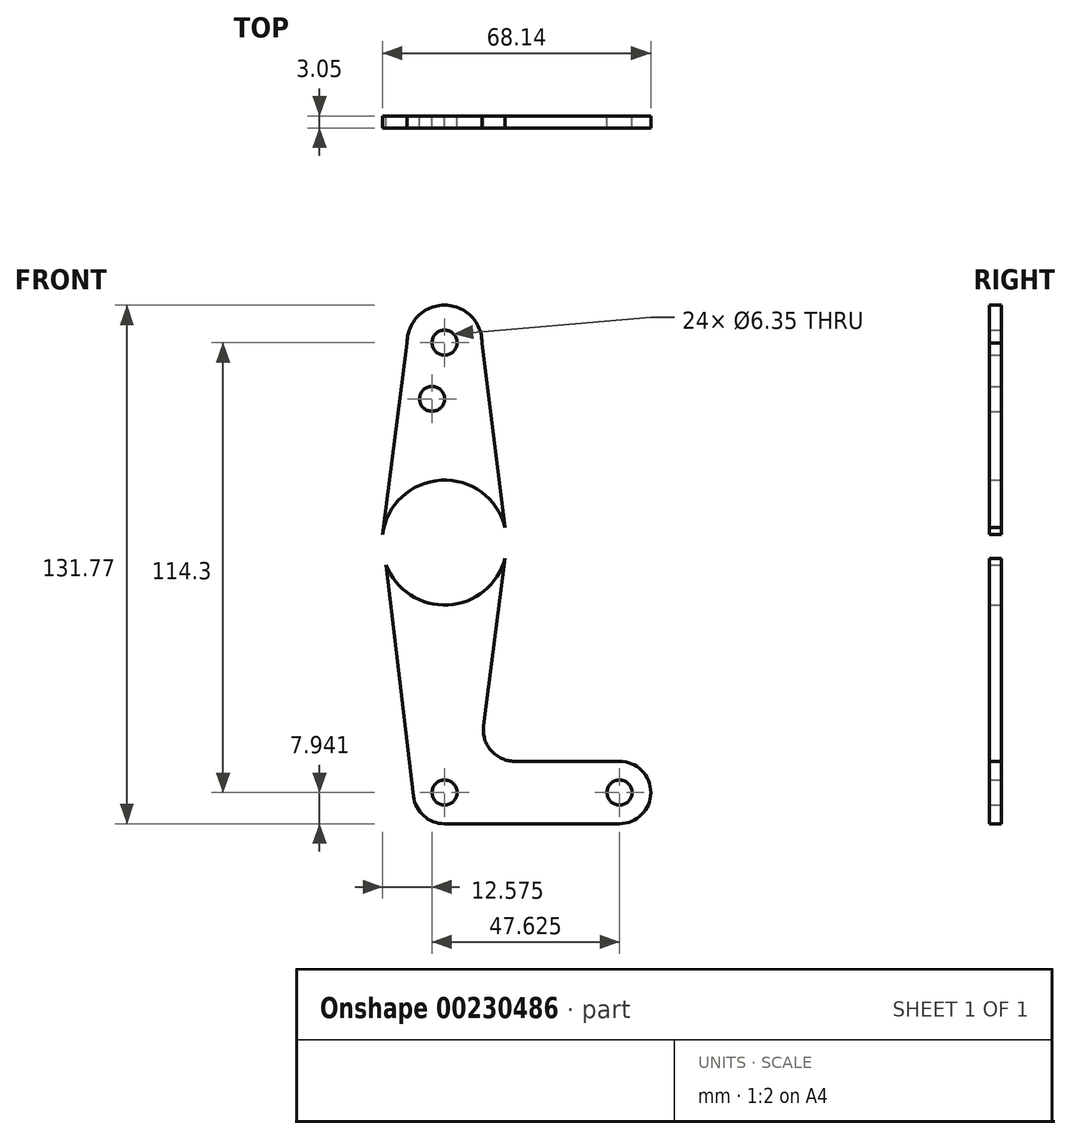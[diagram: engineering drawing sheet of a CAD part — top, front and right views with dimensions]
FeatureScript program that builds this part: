
annotation { "Feature Type Name" : "Feature", "Feature Type Description" : "" }
export const myFeature = defineFeature(function(context is Context, id is Id, definition is map)
    precondition{}
    {
        {
            var Q0;
            Q0=qCreatedBy(makeId("Front.planeOp"),FACE);
            var sketch = newSketch(context, id + "F0", { "sketchPlane" : qUnion([Q0])});
            skLineSegment(sketch, "E0", {"start": v(0, 63.21) * mm, "end": v(0, -51.09) * mm});
            skLineSegment(sketch, "E1", {"start": v(0, -51.09) * mm, "end": v(44.45, -51.09) * mm});
            skCircle(sketch, "E2", {"center": v(0, 63.21) * mm, "radius": 3.18 * mm});
            skCircle(sketch, "E3", {"center": v(0, -51.09) * mm, "radius": 3.18 * mm});
            skCircle(sketch, "E4", {"center": v(44.45, -51.09) * mm, "radius": 7.94 * mm});
            skCircle(sketch, "E5", {"center": v(44.45, -51.09) * mm, "radius": 3.18 * mm});
            skLineSegment(sketch, "E6", {"start": v(0, -51.09) * mm, "end": v(0, 12.41) * mm});
            skCircle(sketch, "E7", {"center": v(0, 12.41) * mm, "radius": 15.88 * mm});
            skCircle(sketch, "E8", {"center": v(0, 12.41) * mm, "radius": 3.18 * mm});
            skCircle(sketch, "E9", {"center": v(0, -51.09) * mm, "radius": 7.94 * mm});
            skCircle(sketch, "E10", {"center": v(0, 63.21) * mm, "radius": 9.53 * mm});
            skLineSegment(sketch, "E11", {"start": v(-9.52, 63.15) * mm, "end": v(-15.75, 14.42) * mm});
            skLineSegment(sketch, "E12", {"start": v(9.52, 63.15) * mm, "end": v(15.87, 12.45) * mm});
            skLineSegment(sketch, "E13", {"start": v(15.87, 12.45) * mm, "end": v(9.92, -34.2) * mm});
            skLineSegment(sketch, "E14", {"start": v(-15.75, 14.42) * mm, "end": v(-7.88, -52.02) * mm});
            skLineSegment(sketch, "E15", {"start": v(17.8, -43.15) * mm, "end": v(44.45, -43.15) * mm});
            skLineSegment(sketch, "E16", {"start": v(0, -59.03) * mm, "end": v(44.45, -59.03) * mm});
            skLineSegment(sketch, "E17", {"start": v(0, 12.41) * mm, "end": v(0, 48.94) * mm});
            skCircle(sketch, "E18", {"center": v(-3.17, 48.94) * mm, "radius": 3.18 * mm});
            skPoint(sketch, "E19.newPointB", {"position": v(0, -43.15) * mm});
            skArc(sketch, "E19.filletArc", {"start": v(9.92, -34.2) * mm, "mid": v(11.84, -40.45) * mm, "end": v(17.8, -43.15) * mm});
            skSolve(sketch);
        }
        {
            var Q0;
            {var subQ0=sQuery(id+"F0.wireOp",EDGE,"E11");Q0=makeQuery(id+"F0.imprint","IMPRINT",FACE,{"disambiguationData":[TD([[makeQuery(id+"F0.imprint","IMPRINT",EDGE,{"derivedFrom":subQ0}),1.0]])]});}
            var Q1;
            {var subQ0=sQuery(id+"F0.wireOp",EDGE,"E12");var subQ3=sQuery(id+"F0.wireOp",EDGE,"E7");var subQ4=makeQuery(id+"F0.imprint","INTERSECT",VERTEX,{"derivedFrom":[subQ3,subQ0]});Q1=makeQuery(id+"F0.imprint","IMPRINT",FACE,{"disambiguationData":[TD([[makeQuery(id+"F0.imprint","IMPRINT",EDGE,{"disambiguationData":[TD([[subQ4,-1.0]])],"derivedFrom":subQ3}),-1.0]])]});}
            var Q2;
            {var subQ1=sQuery(id+"F0.wireOp",EDGE,"E6");var subQ6=sQuery(id+"F0.wireOp",EDGE,"E7");var subQ11=makeQuery(id+"F0.imprint","INTERSECT",VERTEX,{"derivedFrom":[subQ1,subQ6]});Q2=makeQuery(id+"F0.imprint","IMPRINT",FACE,{"disambiguationData":[TD([[makeQuery(id+"F0.imprint","IMPRINT",EDGE,{"disambiguationData":[TD([[subQ11,-1.0]])],"derivedFrom":subQ1}),-1.0]])]});}
            var Q3;
            {var subQ1=sQuery(id+"F0.wireOp",EDGE,"E6");var subQ6=sQuery(id+"F0.wireOp",EDGE,"E7");var subQ8=makeQuery(id+"F0.imprint","INTERSECT",VERTEX,{"derivedFrom":[subQ1,subQ6]});Q3=makeQuery(id+"F0.imprint","IMPRINT",FACE,{"disambiguationData":[TD([[makeQuery(id+"F0.imprint","IMPRINT",EDGE,{"disambiguationData":[TD([[subQ8,-1.0]])],"derivedFrom":subQ1}),1.0]])]});}
            var Q4;
            {var subQ3=sQuery(id+"F0.wireOp",EDGE,"E7");var subQ5=sQuery(id+"F0.wireOp",EDGE,"E14");var subQ7=makeQuery(id+"F0.imprint","INTERSECT",VERTEX,{"derivedFrom":[subQ3,subQ5]});Q4=makeQuery(id+"F0.imprint","IMPRINT",FACE,{"disambiguationData":[TD([[makeQuery(id+"F0.imprint","IMPRINT",EDGE,{"disambiguationData":[TD([[subQ7,-1.0]])],"derivedFrom":subQ3}),-1.0]])]});}
            var Q5;
            {var subQ3=sQuery(id+"F0.wireOp",EDGE,"E7");var subQ5=sQuery(id+"F0.wireOp",EDGE,"E13");var subQ7=makeQuery(id+"F0.imprint","INTERSECT",VERTEX,{"derivedFrom":[subQ3,subQ5]});Q5=makeQuery(id+"F0.imprint","IMPRINT",FACE,{"disambiguationData":[TD([[makeQuery(id+"F0.imprint","IMPRINT",EDGE,{"disambiguationData":[TD([[subQ7,1.0]])],"derivedFrom":subQ3}),-1.0]])]});}
            var Q6;
            {var subQ5=sQuery(id+"F0.wireOp",EDGE,"E1");var subQ7=sQuery(id+"F0.wireOp",EDGE,"E4");var subQ9=makeQuery(id+"F0.imprint","INTERSECT",VERTEX,{"derivedFrom":[subQ5,subQ7]});Q6=makeQuery(id+"F0.imprint","IMPRINT",FACE,{"disambiguationData":[TD([[makeQuery(id+"F0.imprint","IMPRINT",EDGE,{"disambiguationData":[TD([[subQ9,1.0]])],"derivedFrom":subQ5}),1.0]])]});}
            var Q7;
            {var subQ0=sQuery(id+"F0.wireOp",EDGE,"E15");var subQ3=sQuery(id+"F0.wireOp",EDGE,"E13");var subQ5=makeQuery(id+"F0.imprint","INTERSECT",VERTEX,{"derivedFrom":[subQ3,subQ0]});Q7=makeQuery(id+"F0.imprint","IMPRINT",FACE,{"disambiguationData":[TD([[makeQuery(id+"F0.imprint","IMPRINT",EDGE,{"disambiguationData":[TD([[subQ5,-1.0]])],"derivedFrom":subQ3}),-1.0]])]});}
            var Q8;
            {var subQ5=sQuery(id+"F0.wireOp",EDGE,"E16");Q8=makeQuery(id+"F0.imprint","IMPRINT",FACE,{"disambiguationData":[TD([[makeQuery(id+"F0.imprint","IMPRINT",EDGE,{"derivedFrom":subQ5}),1.0]])]});}
            var Q9;
            Q9=makeQuery(id+"F0.imprint","IMPRINT",FACE,{"disambiguationData":[TD([[makeQuery(id+"F0.imprint","IMPRINT",EDGE,{"derivedFrom":sQuery(id+"F0.wireOp",EDGE,"E5")}),-1.0]])]});
            var Q10;
            Q10=makeQuery(id+"F0.imprint","IMPRINT",FACE,{"disambiguationData":[TD([[makeQuery(id+"F0.imprint","IMPRINT",EDGE,{"derivedFrom":sQuery(id+"F0.wireOp",EDGE,"E2")}),-1.0]])]});
            var Q11;
            {var subQ0=sQuery(id+"F0.wireOp",EDGE,"E3");var subQ1=sQuery(id+"F0.wireOp",EDGE,"E1");var subQ2=makeQuery(id+"F0.imprint","INTERSECT",VERTEX,{"derivedFrom":[subQ1,subQ0]});Q11=makeQuery(id+"F0.imprint","IMPRINT",FACE,{"disambiguationData":[TD([[makeQuery(id+"F0.imprint","IMPRINT",EDGE,{"disambiguationData":[TD([[subQ2,-1.0]])],"derivedFrom":subQ1}),1.0]])]});}
            var Q12;
            {var subQ4=sQuery(id+"F0.wireOp",EDGE,"E3");var subQ6=sQuery(id+"F0.wireOp",EDGE,"E1");var subQ7=makeQuery(id+"F0.imprint","INTERSECT",VERTEX,{"derivedFrom":[subQ6,subQ4]});Q12=makeQuery(id+"F0.imprint","IMPRINT",FACE,{"disambiguationData":[TD([[makeQuery(id+"F0.imprint","IMPRINT",EDGE,{"disambiguationData":[TD([[subQ7,-1.0]])],"derivedFrom":subQ6}),-1.0]])]});}
            extrude(context, id + "F1", {"entities" : qUnion([Q0, Q1, Q2, Q3, Q4, Q5, Q6, Q7, Q8, Q9, Q10, Q11, Q12]), "depth" : 3.05 * mm});
        }
    });
